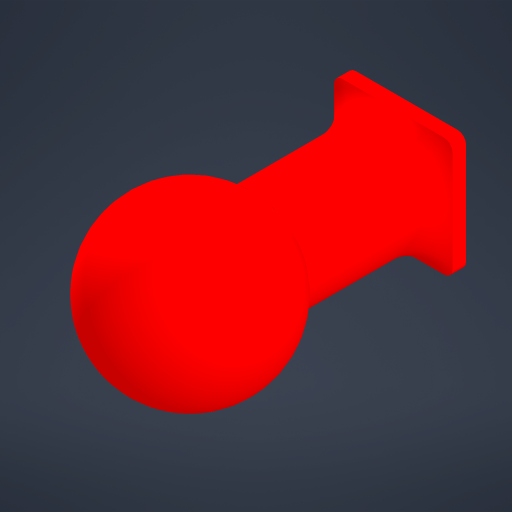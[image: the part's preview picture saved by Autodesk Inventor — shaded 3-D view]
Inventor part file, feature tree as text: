
AUTODESK INVENTOR PART (.ipt)
format: ipt  version: 2023.4 (Build 274418000, 418)  size: 359,936 bytes
history: native  units: mm
features: extrude x3, fillet x3, other x3, plane x2, sketch x2, revolve x1, reference x1, projected_geometry x1
ambient origin geometry x8: Origin, YZ Plane, XZ Plane, XY Plane, X Axis, Y Axis, Z Axis, Center Point
bodies: Solid1 (feature_tree)
feature tree (16):
  plane  "Work Plane1"
  extrude  "Extrusion1"  Depth=2.5mm TaperAngle=0.0deg
  extrude  "Extrusion2"  Depth=30.0mm
  fillet  "Fillet1"  Radius=75.0mm
  extrude  "Extrusion3"  Depth=15.0mm
  fillet  "Fillet2"  Radius=50.0mm
  plane  "Work Plane2"
  revolve  "Revolution1"  [1 undecoded]
  fillet  "Fillet3"  [1 undecoded]
  sketch  "Sketch3"  dims[d8=1.5mm d9=0.0mm d10=2.5mm d11=0.0mm]
  sketch  "Sketch4"  dims[d12=2.5mm d13=30.0mm d14=75.0mm d15=0.0mm d16=15.0mm d17=50.0mm d18=50.0mm d19=90.0deg d20=50.0mm d21=50.0mm d22=35.0mm d23=35.0mm d24=40.0mm d26=360.0deg d28=10.0mm]
  reference  "Reference2"
  projected_geometry  "Projected Loop3"
  other  "<path>\Projects\Project Protocube\Protocube\CAD, STL, OBJ Files\1 CAD\Cube 1x1 V5.iam"
  other  "Cube 1x1 V5.iam"
  other  "Cube 1x1 Top V5 Closed:1"
note: 2 required parameter values undecoded (feature->parameter linkage not recoverable at this tier; creation-order binding heuristic only, values carry confidence <= 0.55)
note: 1 file-system path scrubbed to <path> (originals preserved in map.json)